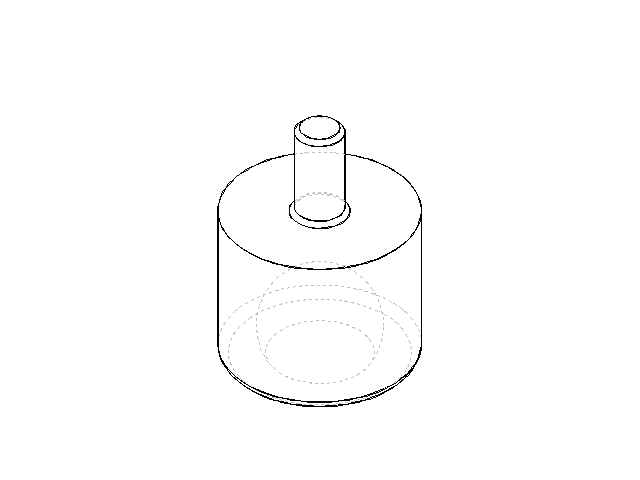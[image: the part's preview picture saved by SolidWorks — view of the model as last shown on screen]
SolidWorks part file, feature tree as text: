
SOLIDWORKS PART (.sldprt)
format: sldprt  version: not decoded by parser v0  size: 121,856 bytes
history: native  units: mm
features: plane x3, sketch x2, chamfer x2, material x1, revolve x1, extrude x1, fillet x1 (+9 scaffold rows collapsed)
feature tree (20):
  scaffold x9  (default folders/planes/origin — collapsed)
  material  "Material <not specified>"
  plane  "Face"
  plane  "Dessus"
  plane  "Droite"
  sketch  "Esquisse1"  dims[c1.D2=6.25mm c1.D1=10.0mm c2.D2=10.0mm c2.D3=6.25mm c2.D4=20.0mm c3.D3=6.25mm c3.D4=20.0mm c3.D5=3.0mm]
  revolve  "Révolution1"  Angle=360deg
  sketch  "Esquisse2"  dims[D1=5.0mm]
  extrude  "Extrusion1"  Depth=10mm
  fillet  "Congé1"  Radius=1mm
  chamfer  "Chanfrein1"  Distance=0.5mm Angle=45deg
  chamfer  "Congé2"  Distance=0.5mm
decode coverage: 7 of 7 modeling features carry decoded parameters
note: suppression state not decoded; provenance and decode notes live in map.json
